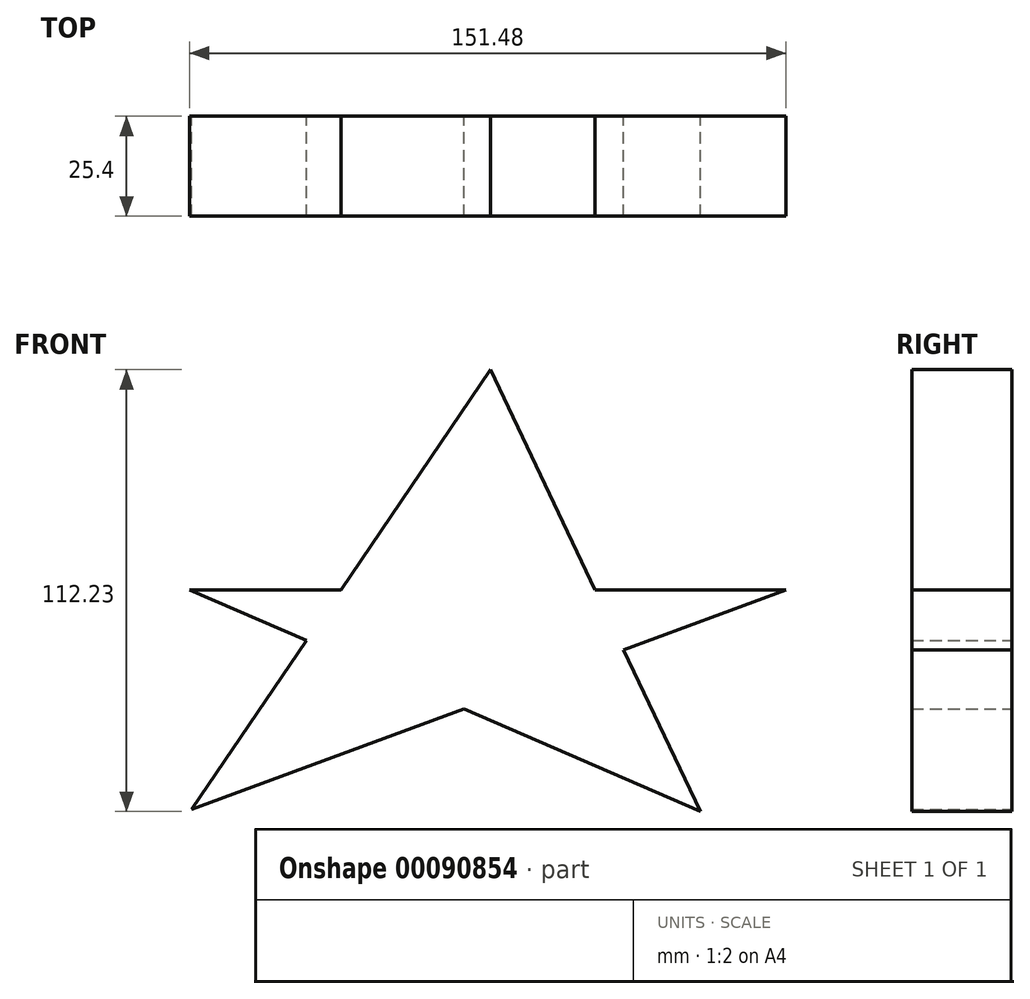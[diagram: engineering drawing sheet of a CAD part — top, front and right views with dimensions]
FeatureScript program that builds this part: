
annotation { "Feature Type Name" : "Feature", "Feature Type Description" : "" }
export const myFeature = defineFeature(function(context is Context, id is Id, definition is map)
    precondition{}
    {
        {
            var Q0;
            Q0=qCreatedBy(makeId("Front.planeOp"),FACE);
            var sketch = newSketch(context, id + "F0", { "sketchPlane" : qUnion([Q0])});
            skLineSegment(sketch, "E0", {"start": v(0, 55.94) * mm, "end": v(-75.97, -55.82) * mm});
            skLineSegment(sketch, "E1", {"start": v(-75.97, -55.82) * mm, "end": v(75.05, 0) * mm});
            skLineSegment(sketch, "E2", {"start": v(75.05, 0) * mm, "end": v(-76.43, 0) * mm});
            skLineSegment(sketch, "E3", {"start": v(-76.43, 0) * mm, "end": v(53.34, -56.29) * mm});
            skLineSegment(sketch, "E4", {"start": v(53.34, -56.29) * mm, "end": v(0, 55.94) * mm});
            skSolve(sketch);
        }
        {
            var Q0;
            {var subQ0=sQuery(id+"F0.wireOp",EDGE,"E4");var subQ1=sQuery(id+"F0.wireOp",EDGE,"E0");var subQ2=makeQuery(id+"F0.imprint","INTERSECT",VERTEX,{"derivedFrom":[subQ1,subQ0]});Q0=makeQuery(id+"F0.imprint","IMPRINT",FACE,{"disambiguationData":[TD([[makeQuery(id+"F0.imprint","IMPRINT",EDGE,{"disambiguationData":[TD([[subQ2,-1.0]])],"derivedFrom":subQ1}),1.0]])]});}
            var Q1;
            {var subQ0=sQuery(id+"F0.wireOp",EDGE,"E2");var subQ1=sQuery(id+"F0.wireOp",EDGE,"E1");var subQ2=makeQuery(id+"F0.imprint","INTERSECT",VERTEX,{"derivedFrom":[subQ1,subQ0]});Q1=makeQuery(id+"F0.imprint","IMPRINT",FACE,{"disambiguationData":[TD([[makeQuery(id+"F0.imprint","IMPRINT",EDGE,{"disambiguationData":[TD([[subQ2,1.0]])],"derivedFrom":subQ1}),1.0]])]});}
            var Q2;
            {var subQ0=sQuery(id+"F0.wireOp",EDGE,"E2");var subQ1=sQuery(id+"F0.wireOp",EDGE,"E0");var subQ2=makeQuery(id+"F0.imprint","INTERSECT",VERTEX,{"derivedFrom":[subQ1,subQ0]});Q2=makeQuery(id+"F0.imprint","IMPRINT",FACE,{"disambiguationData":[TD([[makeQuery(id+"F0.imprint","IMPRINT",EDGE,{"disambiguationData":[TD([[subQ2,-1.0]])],"derivedFrom":subQ1}),-1.0]])]});}
            var Q3;
            {var subQ0=sQuery(id+"F0.wireOp",EDGE,"E3");var subQ1=sQuery(id+"F0.wireOp",EDGE,"E1");var subQ2=makeQuery(id+"F0.imprint","INTERSECT",VERTEX,{"derivedFrom":[subQ1,subQ0]});Q3=makeQuery(id+"F0.imprint","IMPRINT",FACE,{"disambiguationData":[TD([[makeQuery(id+"F0.imprint","IMPRINT",EDGE,{"disambiguationData":[TD([[subQ2,-1.0]])],"derivedFrom":subQ1}),-1.0]])]});}
            var Q4;
            {var subQ1=sQuery(id+"F0.wireOp",EDGE,"E0");var subQ5=sQuery(id+"F0.wireOp",EDGE,"E2");var subQ6=makeQuery(id+"F0.imprint","INTERSECT",VERTEX,{"derivedFrom":[subQ1,subQ5]});Q4=makeQuery(id+"F0.imprint","IMPRINT",FACE,{"disambiguationData":[TD([[makeQuery(id+"F0.imprint","IMPRINT",EDGE,{"disambiguationData":[TD([[subQ6,-1.0]])],"derivedFrom":subQ1}),1.0]])]});}
            var Q5;
            {var subQ0=sQuery(id+"F0.wireOp",EDGE,"E1");var subQ1=sQuery(id+"F0.wireOp",EDGE,"E0");var subQ2=makeQuery(id+"F0.imprint","INTERSECT",VERTEX,{"derivedFrom":[subQ1,subQ0]});Q5=makeQuery(id+"F0.imprint","IMPRINT",FACE,{"disambiguationData":[TD([[makeQuery(id+"F0.imprint","IMPRINT",EDGE,{"disambiguationData":[TD([[subQ2,1.0]])],"derivedFrom":subQ1}),1.0]])]});}
            extrude(context, id + "F1", {"entities" : qUnion([Q0, Q1, Q2, Q3, Q4, Q5]), "depth" : 25.4 * mm});
        }
    });
